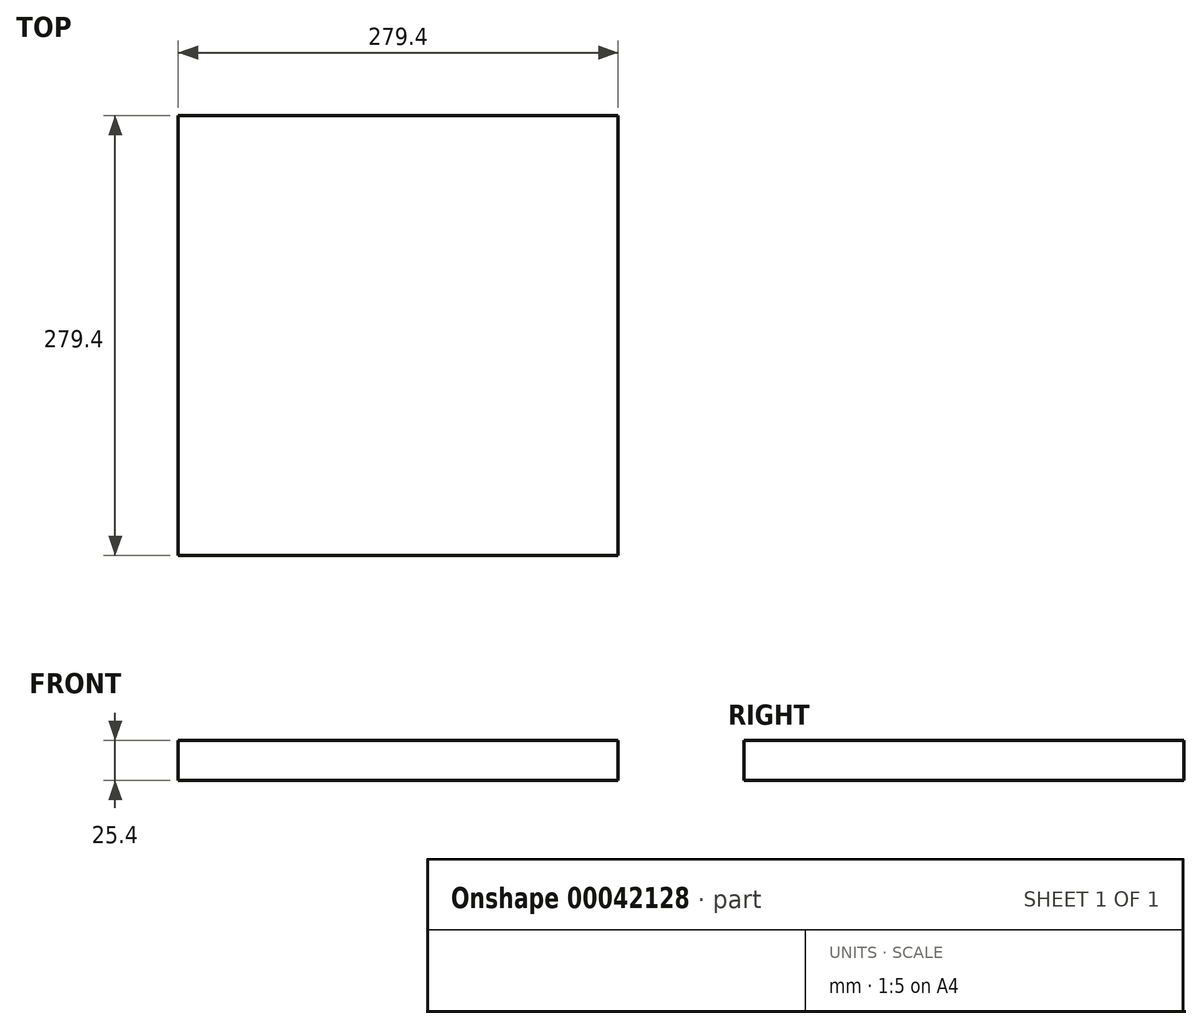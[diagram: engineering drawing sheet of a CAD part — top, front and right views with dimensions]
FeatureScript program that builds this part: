
annotation { "Feature Type Name" : "Feature", "Feature Type Description" : "" }
export const myFeature = defineFeature(function(context is Context, id is Id, definition is map)
    precondition{}
    {
        {
            var Q0;
            Q0=qCreatedBy(makeId("Top.planeOp"),FACE);
            var sketch = newSketch(context, id + "F0", { "sketchPlane" : qUnion([Q0])});
            skLineSegment(sketch, "E0.bottom", {"start": v(-139.7, -139.7) * mm, "end": v(139.7, -139.7) * mm});
            skLineSegment(sketch, "E0.top", {"start": v(-139.7, 139.7) * mm, "end": v(139.7, 139.7) * mm});
            skLineSegment(sketch, "E0.left", {"start": v(-139.7, -139.7) * mm, "end": v(-139.7, 139.7) * mm});
            skLineSegment(sketch, "E0.right", {"start": v(139.7, -139.7) * mm, "end": v(139.7, 139.7) * mm});
            skPoint(sketch, "E0.middle", {"position": v(0, 0) * mm});
            skSolve(sketch);
        }
        {
            var Q0;
            Q0=makeQuery(id+"F0.imprint","IMPRINT",FACE,{"disambiguationData":[TD([[makeQuery(id+"F0.imprint","IMPRINT",EDGE,{"derivedFrom":sQuery(id+"F0.wireOp",EDGE,"E0.bottom")}),1.0]])]});
            extrude(context, id + "F1", {"entities" : qUnion([Q0]), "depth" : 25.4 * mm});
        }
        {
            var Q0;
            Q0=makeQuery(id+"F1.opExtrude","CAP_FACE",FACE,{"disambiguationData":[OSD([sQuery(id+"F0.wireOp",EDGE,"E0.bottom"),sQuery(id+"F0.wireOp",EDGE,"E0.top"),sQuery(id+"F0.wireOp",EDGE,"E0.left"),sQuery(id+"F0.wireOp",EDGE,"E0.right")])],"isStart":false});
            var sketch = newSketch(context, id + "F2", { "sketchPlane" : qUnion([Q0])});
            skCircle(sketch, "E1", {"center": v(0, 0) * mm, "radius": 114.21 * mm});
            skSolve(sketch);
        }
        {
            var Q0;
            Q0=makeQuery(id+"F2.imprint","IMPRINT",FACE,{"disambiguationData":[TD([[makeQuery(id+"F2.imprint","IMPRINT",EDGE,{"derivedFrom":sQuery(id+"F2.wireOp",EDGE,"E1")}),1.0]])]});
            extrude(context, id + "F3", {"entities" : qUnion([Q0]), "operationType" : NewBodyOperationType.REMOVE, "oppositeDirection" : true, "depth" : 3.17 * mm});
        }
        {
            var Q0;
            Q0=makeQuery(id+"F3.boolean.opBoolean","COPY",FACE,{"derivedFrom":makeQuery(id+"F3.opExtrude","CAP_FACE",FACE,{"disambiguationData":[OSD([sQuery(id+"F2.wireOp",EDGE,"E1")])],"isStart":false})});
            var sketch = newSketch(context, id + "F4", { "sketchPlane" : qUnion([Q0])});
            skCircle(sketch, "E2", {"center": v(0, 0) * mm, "radius": 95.16 * mm});
            skSolve(sketch);
        }
        {
            var Q0;
            Q0=makeQuery(id+"F4.imprint","IMPRINT",FACE,{"disambiguationData":[TD([[makeQuery(id+"F4.imprint","IMPRINT",EDGE,{"derivedFrom":sQuery(id+"F4.wireOp",EDGE,"E2")}),1.0]])]});
            extrude(context, id + "F5", {"entities" : qUnion([Q0]), "operationType" : NewBodyOperationType.REMOVE, "oppositeDirection" : true, "depth" : 22.22 * mm});
        }
        {
            var Q0;
            Q0 = qSketchRegion(id + "F0", true);
            extrude(context, id + "F6", {"entities" : qUnion([Q0]), "operationType" : NewBodyOperationType.ADD, "depth" : 25.4 * mm});
        }
    });
